# Revit family: SB1824-A30_4
name_source: partatom
category: Mechanical Equipment
revit_build: Autodesk Revit 2018 (Build: 20170223_1515(x64)
units: mm (PartAtom-declared; Revit-internal decimal feet)

## family parameters
Always vertical = Yes
Cut with Voids When Loaded = No
Part Type = Normal
Room Calculation Point = No
Round Connector Dimension = Use Diameter
Shared = No
Work Plane-Based = No

## types (1)
- SB1824-A30/4
    Cable Length (m) = As Per Specification
    Cable Type = HO7RN
    Coupling bracket = 1.4408 / ASTM / AISI CF - 8M
    Description = The reliable, energy efficient low-speed submersible unit can be used in a wide range of applications in wastewater treatment plants. This is Sulzer’s standard range of low-speed mixers; economical without compromising on the reliable design.
    Fasteners = Stainless steel 1.4401 (AISI 316)
    Manufacturer = Sulzer
    Mixing Flow = up to 4.3m3/s
    Model = Type ABS SB
    Motor Housing = EN-GJS-400-18/ ASTM A 536, 60-40-18
    Motor Power (kW) = P1=4
    Motor Shaft = 1.0006, ASTM, AISI A276 Gr.65 / 1,7225 fully encapsulated (42CrMo4)
    Product Specification Link = https://www.sulzer.com
    Propeller = PUR
    Rated Current (A) = 9
    Rated Voltage (V) = 400
    motor speed (r/min) = 1424
    propeller Speed (r/min) = 63

## geometry (parser evidence)
native form markers: Revolve x1, Sweep x3
no freeform markers — native parametric forms only
